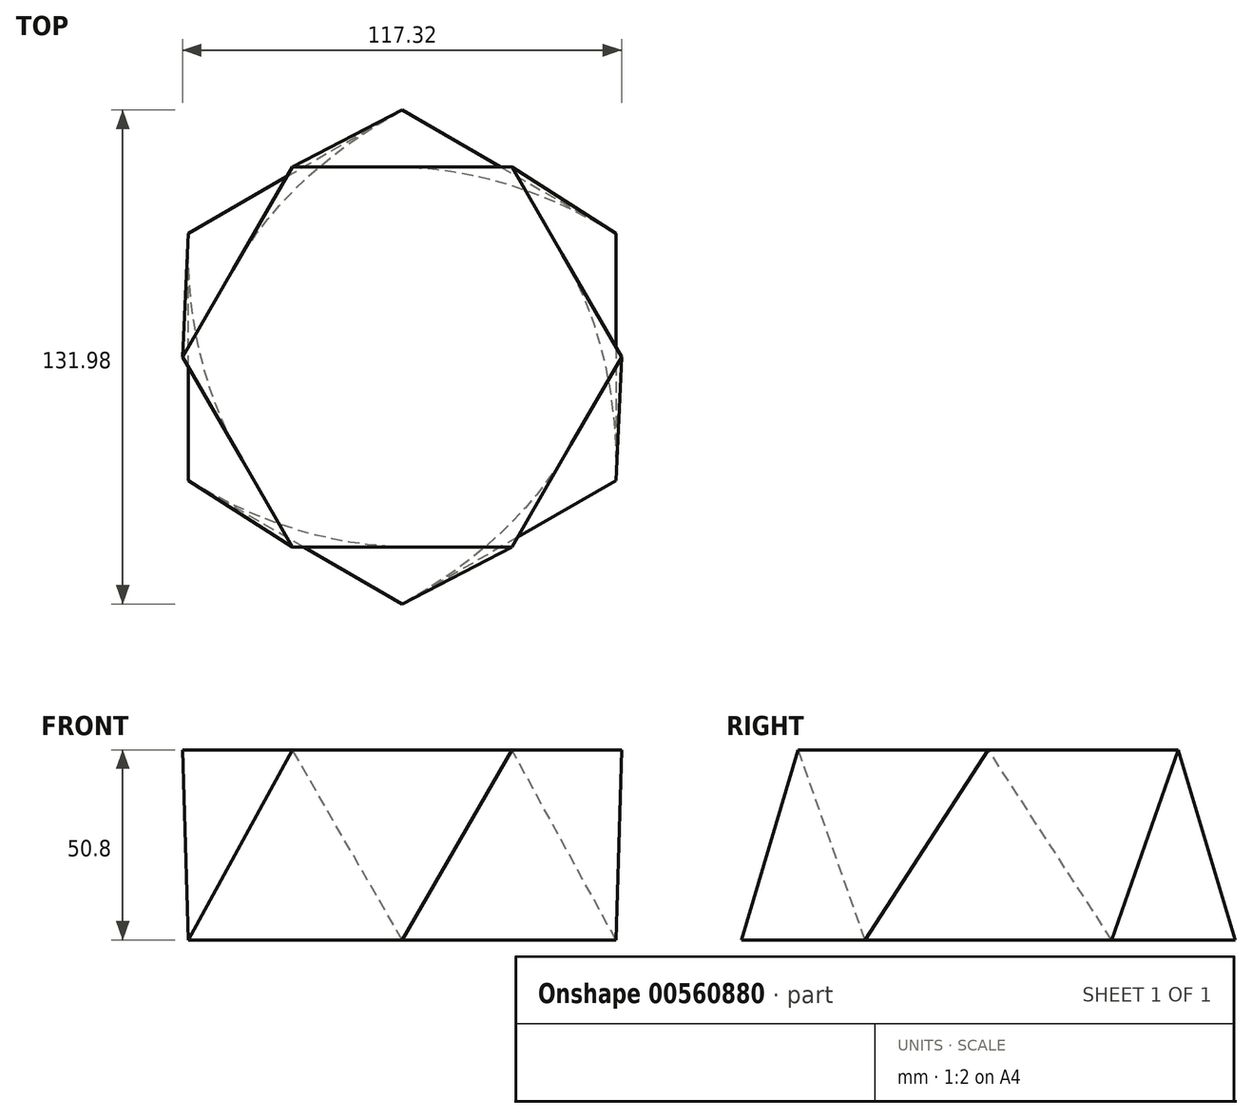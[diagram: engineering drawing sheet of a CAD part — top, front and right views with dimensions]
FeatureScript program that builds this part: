
annotation { "Feature Type Name" : "Feature", "Feature Type Description" : "" }
export const myFeature = defineFeature(function(context is Context, id is Id, definition is map)
    precondition{}
    {
        {
            var Q0;
            Q0=qCreatedBy(makeId("Top.planeOp"),FACE);
            var sketch = newSketch(context, id + "F0", { "sketchPlane" : qUnion([Q0])});
            skCircle(sketch, "E0.cCircle", {"center": v(0, 0) * mm, "radius": 57.15 * mm, "construction": true});
            skLineSegment(sketch, "E0.0", {"start": v(57.15, 33) * mm, "end": v(57.15, -33) * mm});
            skLineSegment(sketch, "E0.1", {"start": v(57.15, -33) * mm, "end": v(0, -66) * mm});
            skLineSegment(sketch, "E0.2", {"start": v(0, -66) * mm, "end": v(-57.15, -33) * mm});
            skLineSegment(sketch, "E0.3", {"start": v(-57.15, -33) * mm, "end": v(-57.15, 33) * mm});
            skLineSegment(sketch, "E0.4", {"start": v(-57.15, 33) * mm, "end": v(0, 66) * mm});
            skLineSegment(sketch, "E0.5", {"start": v(0, 66) * mm, "end": v(57.15, 33) * mm});
            skPoint(sketch, "E0.0.midPoint", {"position": v(57.15, 0) * mm});
            skSolve(sketch);
        }
        {
            var Q0;
            Q0=qCreatedBy(makeId("Top.planeOp"),FACE);
            cPlane(context, id + "F1", {"entities" : qUnion([Q0]), "cplaneType" : CPlaneType.OFFSET, "offset" : 50.8 * mm, "width" : 152.4 * mm, "height" : 152.4 * mm});
        }
        {
            var Q0;
            Q0=qCreatedBy(id+"F1.planeOp",FACE);
            var sketch = newSketch(context, id + "F2", { "sketchPlane" : qUnion([Q0])});
            skCircle(sketch, "E1.cCircle", {"center": v(0, 0) * mm, "radius": 50.8 * mm, "construction": true});
            skLineSegment(sketch, "E1.0", {"start": v(58.66, 0) * mm, "end": v(29.33, -50.8) * mm});
            skLineSegment(sketch, "E1.1", {"start": v(29.33, -50.8) * mm, "end": v(-29.33, -50.8) * mm});
            skLineSegment(sketch, "E1.2", {"start": v(-29.33, -50.8) * mm, "end": v(-58.66, 0) * mm});
            skLineSegment(sketch, "E1.3", {"start": v(-58.66, 0) * mm, "end": v(-29.33, 50.8) * mm});
            skLineSegment(sketch, "E1.4", {"start": v(-29.33, 50.8) * mm, "end": v(29.33, 50.8) * mm});
            skLineSegment(sketch, "E1.5", {"start": v(29.33, 50.8) * mm, "end": v(58.66, 0) * mm});
            skPoint(sketch, "E1.0.midPoint", {"position": v(44, -25.4) * mm});
            skSolve(sketch);
        }
        {
            var Q0;
            Q0=makeQuery(id+"F0.imprint","IMPRINT",FACE,{"disambiguationData":[TD([[makeQuery(id+"F0.imprint","IMPRINT",EDGE,{"derivedFrom":sQuery(id+"F0.wireOp",EDGE,"E0.0")}),-1.0]])]});
            var Q1;
            Q1=makeQuery(id+"F2.imprint","IMPRINT",FACE,{"disambiguationData":[TD([[makeQuery(id+"F2.imprint","IMPRINT",EDGE,{"derivedFrom":sQuery(id+"F2.wireOp",EDGE,"E1.0")}),-1.0]])]});
            loft(context, id + "F3", {"sheetProfilesArray" : [{ "sheetProfileEntities" : qUnion([Q0]) }, { "sheetProfileEntities" : qUnion([Q1]) }]});
        }
    });
